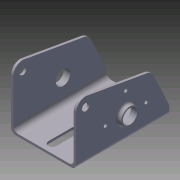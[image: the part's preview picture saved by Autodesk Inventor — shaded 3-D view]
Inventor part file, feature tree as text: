
AUTODESK INVENTOR PART (.ipt)
format: ipt  version: 2011 (Build 150239000, 239)  size: 224,256 bytes
history: native  units: in
note: dims shown in document units (in); Inventor stores cm internally (conversion verified against a paired STEP export)
features: extrude x7, sketch x7, fillet x5, plane x1, mirror x1, reference x1
ambient origin geometry x8: Origin, YZ Plane, XZ Plane, XY Plane, X Axis, Y Axis, Z Axis, Center Point
bodies: Solid1 (feature_tree)
feature tree (22):
  extrude  "Extrusion1"  Depth=0.12in
  fillet  "Fillet1"  Radius=0.12in
  extrude  "Extrusion2"  Depth=3.095in
  fillet  "Fillet2"  [1 undecoded]
  extrude  "Extrusion3"  Depth=0.5in
  fillet  "Fillet3"  Radius=0.375in
  fillet  "Fillet4"  Radius=4.872in
  extrude  "Extrusion4"  Depth=0.25in
  extrude  "Extrusion5"  Depth=0.4466in
  sketch  "Sketch6"  dims[d17=4.872in d18=0.0in d19=0.5in d20=0.5in]
  plane  "Work Plane1"
  mirror  "Mirror1"
  extrude  "Extrusion6"  Depth=0.5in
  fillet  "Fillet5"  Radius=0.5in
  extrude  "Extrusion7"  Depth=0.425in
  sketch  "Sketch1"  dims[d0=3.4in d1=0.12in d2=0.12in]
  sketch  "Sketch2"  dims[d3=0.12in d4=3.095in d5=0.0in]
  sketch  "Sketch3"  dims[d6=4.872in d7=0.0in d8=0.5in d9=0.375in d10=4.872in d11=0.0in]
  sketch  "Sketch4"  dims[d12=0.25in d13=0.25in]
  sketch  "Sketch5"  dims[d15=0.8589in d16=0.4466in]
  sketch  "Sketch7"  dims[d21=0.425in d22=0.425in d23=1.0in d24=0.4625in d25=0.425in d26=0.4253in d27=0.4625in d28=1.217in d29=1.217in d30=1.217in d31=4.872in d32=0.0in d33=0.75in d36=0.9in d37=1.24in d38=2.5in d39=0.215in d40=0.0in d41=0.215in d42=0.0in d43=0.1in d44=1.0in d45=0.0in]
  reference  "Reference1"
note: 1 required parameter value undecoded (feature->parameter linkage not recoverable at this tier; creation-order binding heuristic only, values carry confidence <= 0.55)
